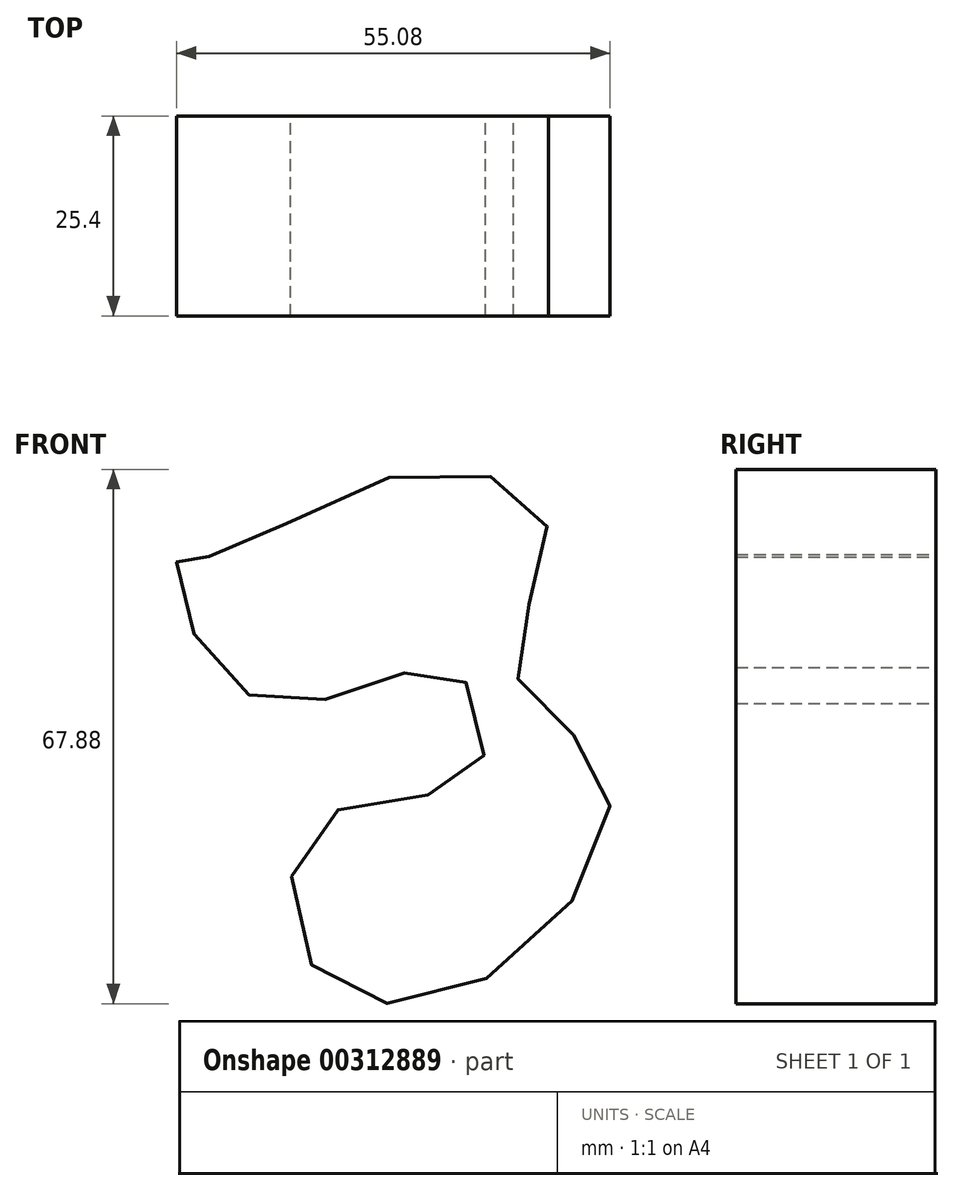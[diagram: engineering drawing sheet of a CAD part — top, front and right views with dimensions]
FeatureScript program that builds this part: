
annotation { "Feature Type Name" : "Feature", "Feature Type Description" : "" }
export const myFeature = defineFeature(function(context is Context, id is Id, definition is map)
    precondition{}
    {
        {
            var Q0;
            Q0=qCreatedBy(makeId("Front.planeOp"),FACE);
            var sketch = newSketch(context, id + "F0", { "sketchPlane" : qUnion([Q0])});
            skFitSpline(sketch, "E0", {"points": [v(-19.87, 27.9) * mm, v(-23.75, 27.88) * mm, v(-18.9, 13.42) * mm, v(-3.63, 10.12) * mm, v(11.58, 12.97) * mm, v(13.74, 0) * mm, v(-5.65, -5.46) * mm, v(-6.26, -24.72) * mm, v(16.77, -24.89) * mm, v(30.49, 0) * mm, v(18.94, 13.5) * mm, v(23.16, 31.24) * mm, v(6.3, 38.72) * mm, v(-19.87, 27.9) * mm]});
            skSolve(sketch);
        }
        {
            var Q0;
            Q0=makeQuery(id+"F0.imprint","IMPRINT",FACE,{"disambiguationData":[TD([[makeQuery(id+"F0.imprint","IMPRINT",EDGE,{"derivedFrom":sQuery(id+"F0.wireOp",EDGE,"E0")}),1.0]])]});
            extrude(context, id + "F1", {"entities" : qUnion([Q0]), "depth" : 25.4 * mm});
        }
    });
